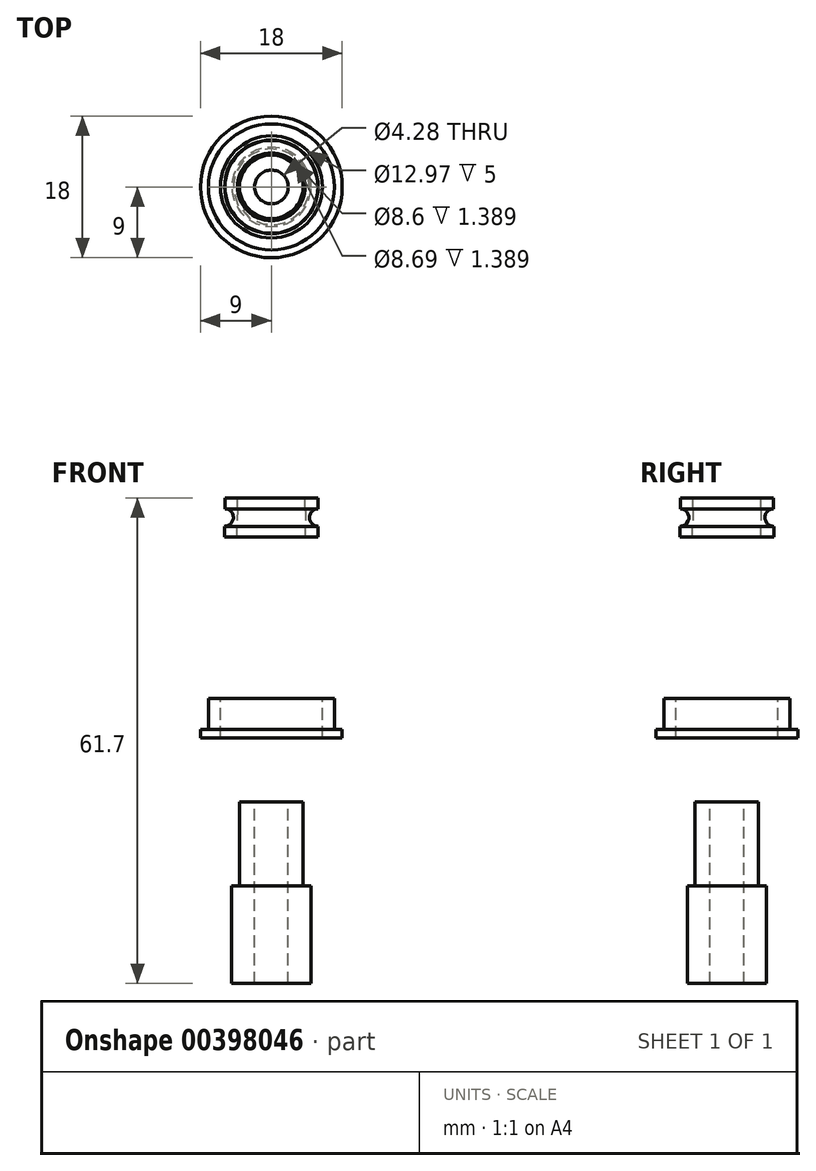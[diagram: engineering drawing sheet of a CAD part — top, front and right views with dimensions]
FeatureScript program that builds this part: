
annotation { "Feature Type Name" : "Feature", "Feature Type Description" : "" }
export const myFeature = defineFeature(function(context is Context, id is Id, definition is map)
    precondition{}
    {
        {
            var Q0;
            Q0=qCreatedBy(makeId("Front.planeOp"),FACE);
            var sketch = newSketch(context, id + "F0", { "sketchPlane" : qUnion([Q0])});
            skLineSegment(sketch, "E0", {"start": v(0, 48.14) * mm, "end": v(0, -38.06) * mm, "construction": true});
            skLineSegment(sketch, "E1", {"start": v(2.14, 6.17) * mm, "end": v(2.14, -16.9) * mm});
            skLineSegment(sketch, "E2", {"start": v(2.14, 6.17) * mm, "end": v(4.04, 6.17) * mm});
            skLineSegment(sketch, "E3", {"start": v(4.04, 6.17) * mm, "end": v(4.04, -4.5) * mm});
            skLineSegment(sketch, "E4", {"start": v(4.04, -4.5) * mm, "end": v(5.04, -4.5) * mm});
            skLineSegment(sketch, "E5", {"start": v(5.04, -4.5) * mm, "end": v(5.04, -16.9) * mm});
            skLineSegment(sketch, "E6", {"start": v(2.14, -16.9) * mm, "end": v(5.04, -16.9) * mm});
            skCircle(sketch, "E7", {"center": v(44.51, -46.48) * mm, "radius": 13.49 * mm});
            skLineSegment(sketch, "E8", {"start": v(8, 19.3) * mm, "end": v(8, 15.4) * mm});
            skLineSegment(sketch, "E9", {"start": v(8, 15.4) * mm, "end": v(9, 15.4) * mm});
            skLineSegment(sketch, "E10", {"start": v(9, 15.4) * mm, "end": v(9, 14.3) * mm});
            skLineSegment(sketch, "E11", {"start": v(0, 19.47) * mm, "end": v(0, 14.47) * mm});
            skPoint(sketch, "E12.orphan", {"position": v(0, 33.12) * mm});
            skLineSegment(sketch, "E13", {"start": v(8, 19.3) * mm, "end": v(6.48, 19.3) * mm});
            skLineSegment(sketch, "E14", {"start": v(6.48, 19.3) * mm, "end": v(6.48, 15.4) * mm});
            skLineSegment(sketch, "E15", {"start": v(8, 15.4) * mm, "end": v(6.48, 15.4) * mm});
            skLineSegment(sketch, "E16", {"start": v(6.48, 15.4) * mm, "end": v(6.48, 14.3) * mm});
            skLineSegment(sketch, "E17", {"start": v(6.48, 14.3) * mm, "end": v(9, 14.3) * mm});
            skLineSegment(sketch, "E18", {"start": v(4.3, 44.8) * mm, "end": v(5.9, 44.8) * mm});
            skLineSegment(sketch, "E19", {"start": v(5.9, 44.8) * mm, "end": v(5.9, 43.4) * mm});
            skLineSegment(sketch, "E20", {"start": v(5.9, 43.4) * mm, "end": v(4.3, 43.4) * mm});
            skLineSegment(sketch, "E21", {"start": v(4.3, 43.4) * mm, "end": v(4.3, 44.8) * mm});
            skLineSegment(sketch, "E22", {"start": v(4.35, 41.18) * mm, "end": v(5.95, 41.18) * mm});
            skLineSegment(sketch, "E23", {"start": v(5.95, 41.18) * mm, "end": v(5.95, 39.8) * mm});
            skLineSegment(sketch, "E24", {"start": v(5.95, 39.8) * mm, "end": v(4.35, 39.8) * mm});
            skLineSegment(sketch, "E25", {"start": v(4.35, 39.8) * mm, "end": v(4.35, 41.18) * mm});
            skLineSegment(sketch, "E26", {"start": v(4.3, 43.4) * mm, "end": v(4.35, 41.18) * mm});
            skArc(sketch, "E27", {"start": v(5.9, 43.4) * mm, "mid": v(4.83, 42.27) * mm, "end": v(5.95, 41.18) * mm});
            skPoint(sketch, "E28.orphan", {"position": v(0, 44.8) * mm});
            skSolve(sketch);
        }
        {
            var Q0;
            Q0=makeQuery(id+"F0.imprint","IMPRINT",FACE,{"disambiguationData":[TD([[makeQuery(id+"F0.imprint","IMPRINT",EDGE,{"derivedFrom":sQuery(id+"F0.wireOp",EDGE,"E8")}),-1.0]])]});
            var Q1;
            Q1=makeQuery(id+"F0.imprint","IMPRINT",FACE,{"disambiguationData":[TD([[makeQuery(id+"F0.imprint","IMPRINT",EDGE,{"derivedFrom":sQuery(id+"F0.wireOp",EDGE,"E9")}),-1.0]])]});
            var Q2;
            Q2=makeQuery(id+"F0.imprint","IMPRINT",FACE,{"disambiguationData":[TD([[makeQuery(id+"F0.imprint","IMPRINT",EDGE,{"derivedFrom":sQuery(id+"F0.wireOp",EDGE,"E1")}),1.0]])]});
            var Q3;
            Q3=makeQuery(id+"F0.imprint","IMPRINT",FACE,{"disambiguationData":[TD([[makeQuery(id+"F0.imprint","IMPRINT",EDGE,{"derivedFrom":sQuery(id+"F0.wireOp",EDGE,"E18")}),-1.0]])]});
            var Q4;
            Q4=makeQuery(id+"F0.imprint","IMPRINT",FACE,{"disambiguationData":[TD([[makeQuery(id+"F0.imprint","IMPRINT",EDGE,{"derivedFrom":sQuery(id+"F0.wireOp",EDGE,"E20")}),1.0]])]});
            var Q5;
            Q5=makeQuery(id+"F0.imprint","IMPRINT",FACE,{"disambiguationData":[TD([[makeQuery(id+"F0.imprint","IMPRINT",EDGE,{"derivedFrom":sQuery(id+"F0.wireOp",EDGE,"E22")}),-1.0]])]});
            var Q6;
            Q6=sQuery(id+"F0.wireOp",EDGE,"E0");
            revolve(context, id + "F1", {"entities" : qUnion([Q0, Q1, Q2, Q3, Q4, Q5]), "axis" : qUnion([Q6]), "revolveType" : RevolveType.FULL});
        }
    });
